# Revit family: Prises verrouillés 380_415V
name_source: partatom
category: Installations électriques
revit_build: Autodesk Revit 2018 (Build: 20170223_1515(x64)
units: mm (PartAtom-declared; Revit-internal decimal feet)

## family parameters
Conserver l'orientation des annotations = Non
Cote de connecteur circulaire = Utiliser le diamètre
Couper avec des vides une fois chargée = Non
Hôte = Face
Partagée = Non
Point de calcul de pièce = Non
Type d'élément = Normal

## types (4) — shared parameters
Couleur caractéristique = rouge
Elévation par défaut = 1000 mm  [stored 3.28084 ft]
Fabricant = Legrand
Famille produit = 0852-P17
Intensité A = 16 A
Position de la Terre h = 6
Prise au standard international pour montage encastré ou saillie avec accessoire permet la connexion d'appareils de puissance = Prise au standard international pour montage encastré ou saillie avec accessoire permet la connexion d'appareils de puissance
Standard CEI ou NFC = CEI
Température maximum d'utilisation = +40
Température minimum d'utilisation = -25
Tension V = 400 V  50/60 Hz  rouge
Type de cerrouillage = verrouillage électromécanique
entraxe de fixation horizontal mm = 91 mm
entraxe de fixation vertical mm = 87 mm
hauteur mm = 105 mm  [stored 0.344488 ft]
largeur mm = 125 mm  [stored 0.410105 ft]
matériau du boitier = plastique
profondeur d'encastrement mm = 81 mm  [stored 0.265748 ft]
profondeur mm = 120 mm  [stored 0.393701 ft]
sans halogène = Oui
type de raccordement = bornes à vis

## per-type parameters (varying)
| type | Description | Modèle | Nombre de pôles | classe de protection IP | résistance aux chocs IK |
| P17 - IP55 - 380/415V-16A -3P+N+T | LG-057322 Prise vérrouillée P17 - IP55 - 380/415V - 16A -3P+T | LG-057322 | 5 | IP55 | 13 |
| P17 - IP55 - 380/415V - 16A -3P+T | LG-057321Prise vérrouillée P17 - IP55 - 380/415V - 16A -3P+T | LG-057321 | 4 | IP55 | 12 |
| P17 - IP44 - 380/415V-16A -3P+N+T | LG-057302 Prise vérrouillée P17 - IP44 - 380/415V-16A -3P+N+T | LG-057302 | 5 | IP44 | 10 |
| P17 - IP44 - 380/415V - 16A -3P+T | LG-057301 Prise vérrouillée P17 - IP44 - 380/415V - 16A -3P+T | LG-057301 | 4 | IP44 | 09 |

note: [stored X ft] marks values corroborated as IEEE doubles in the binary element streams (Revit-internal decimal feet)
